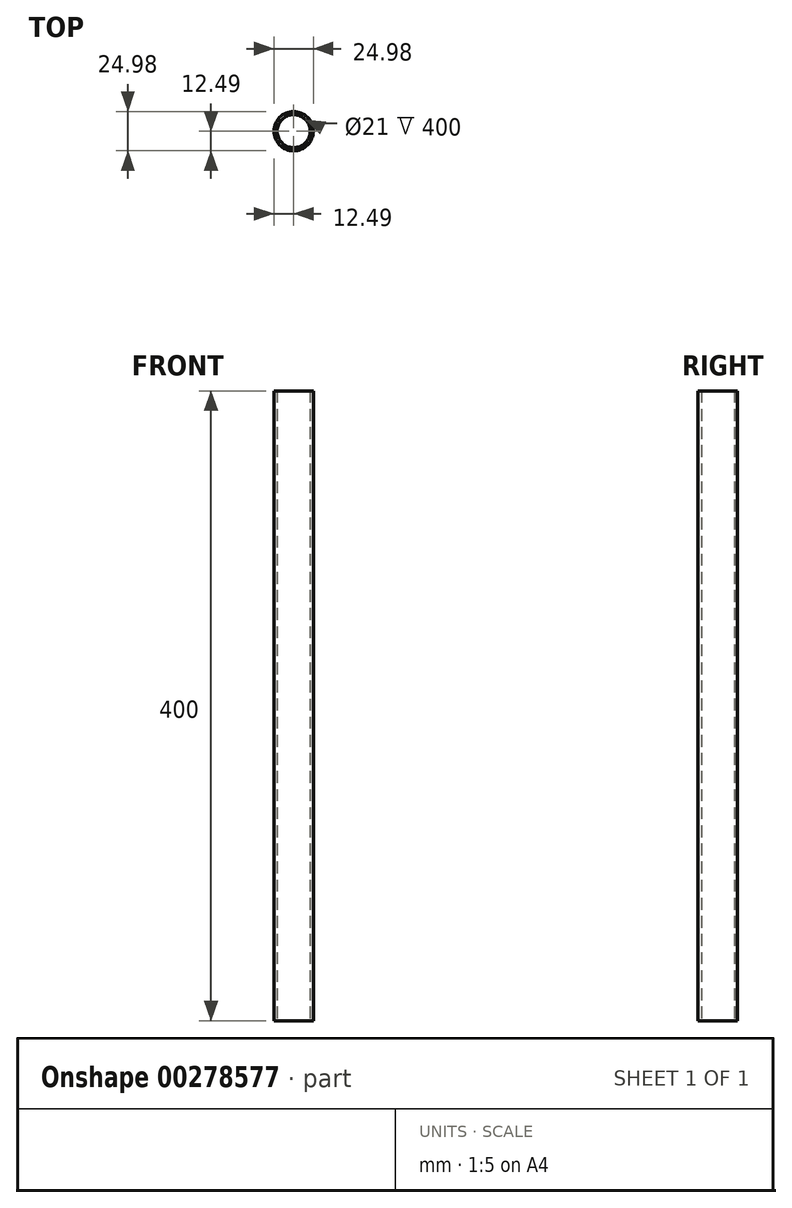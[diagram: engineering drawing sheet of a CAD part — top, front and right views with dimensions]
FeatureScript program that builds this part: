
annotation { "Feature Type Name" : "Feature", "Feature Type Description" : "" }
export const myFeature = defineFeature(function(context is Context, id is Id, definition is map)
    precondition{}
    {
        {
            var Q0;
            Q0=qCreatedBy(makeId("Top.planeOp"),FACE);
            var sketch = newSketch(context, id + "F0", { "sketchPlane" : qUnion([Q0])});
            skCircle(sketch, "E0", {"center": v(0, 0) * mm, "radius": 12.5 * mm});
            skCircle(sketch, "E1", {"center": v(0, 0) * mm, "radius": 10.5 * mm});
            skSolve(sketch);
        }
        {
            var Q0;
            Q0=makeQuery(id+"F0.imprint","IMPRINT",FACE,{"disambiguationData":[TD([[makeQuery(id+"F0.imprint","IMPRINT",EDGE,{"derivedFrom":sQuery(id+"F0.wireOp",EDGE,"E0")}),1.0]])]});
            extrude(context, id + "F1", {"entities" : qUnion([Q0]), "depth" : 200 * mm, "hasSecondDirection" : true, "secondDirectionOppositeDirection" : true, "secondDirectionDepth" : 200 * mm});
        }
    });
